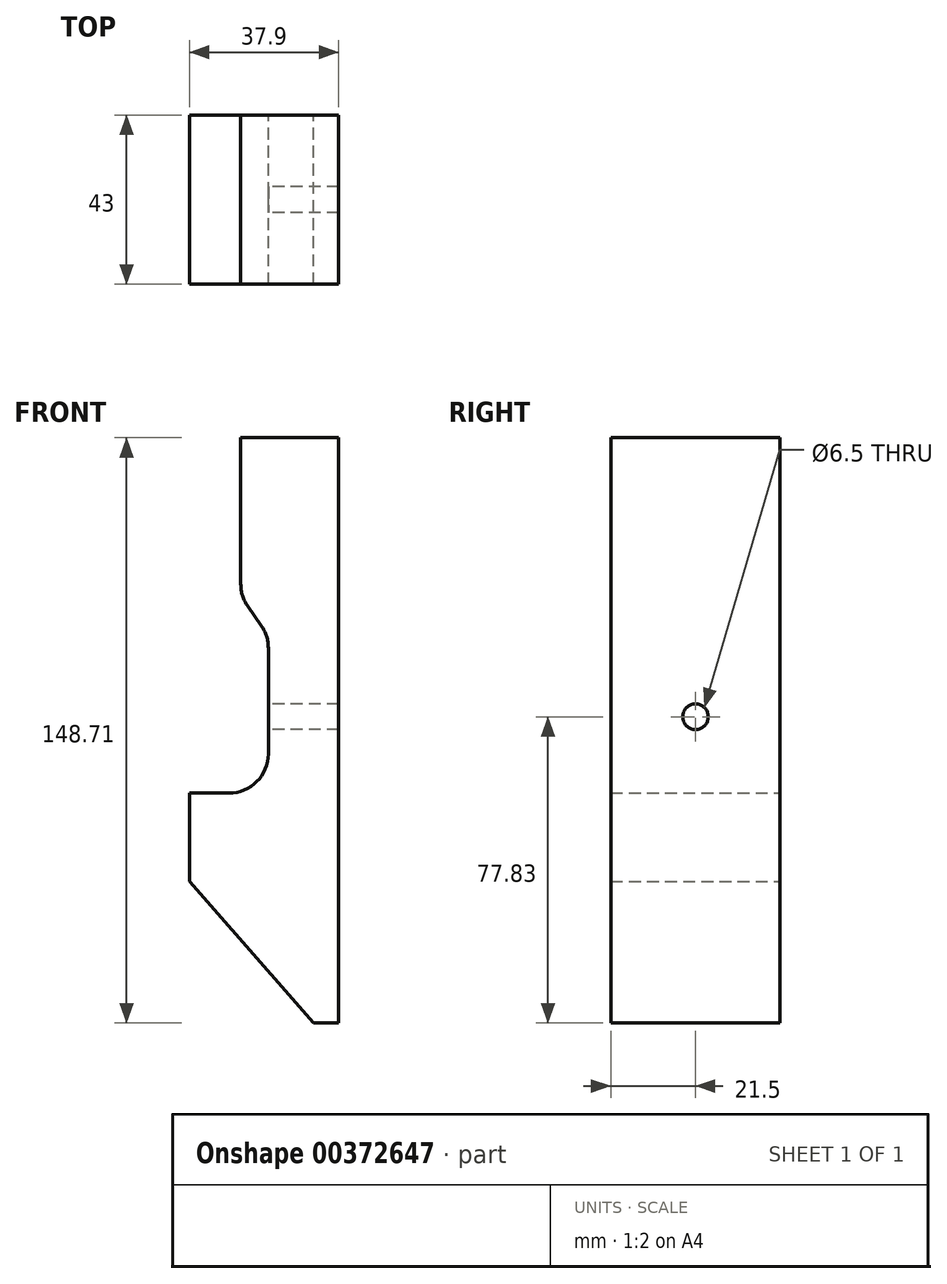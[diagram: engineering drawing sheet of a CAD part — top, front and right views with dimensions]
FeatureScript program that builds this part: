
annotation { "Feature Type Name" : "Feature", "Feature Type Description" : "" }
export const myFeature = defineFeature(function(context is Context, id is Id, definition is map)
    precondition{}
    {
        {
            var Q0;
            Q0=qCreatedBy(makeId("Front.planeOp"),FACE);
            var sketch = newSketch(context, id + "F0", { "sketchPlane" : qUnion([Q0])});
            skLineSegment(sketch, "E0", {"start": v(-20, -19.4) * mm, "end": v(0, -19.4) * mm});
            skLineSegment(sketch, "E1", {"start": v(0, 20.6) * mm, "end": v(-7, 30.6) * mm});
            skLineSegment(sketch, "E2", {"start": v(-7, 30.6) * mm, "end": v(-7, 70.88) * mm});
            skLineSegment(sketch, "E3", {"start": v(-7, 70.88) * mm, "end": v(17.9, 70.88) * mm});
            skLineSegment(sketch, "E4", {"start": v(17.9, 70.88) * mm, "end": v(17.9, -77.83) * mm});
            skLineSegment(sketch, "E5", {"start": v(17.9, -77.83) * mm, "end": v(11.45, -77.83) * mm});
            skLineSegment(sketch, "E6", {"start": v(11.45, -77.83) * mm, "end": v(-20, -41.81) * mm});
            skLineSegment(sketch, "E7", {"start": v(-20, -41.81) * mm, "end": v(-20, -19.4) * mm});
            skLineSegment(sketch, "E8", {"start": v(0, 20.6) * mm, "end": v(0, -19.4) * mm});
            skSolve(sketch);
        }
        {
            var Q0;
            Q0=makeQuery(id+"F0.imprint","IMPRINT",FACE,{"disambiguationData":[TD([[makeQuery(id+"F0.imprint","IMPRINT",EDGE,{"derivedFrom":sQuery(id+"F0.wireOp",EDGE,"E0")}),-1.0]])]});
            extrude(context, id + "F1", {"entities" : qUnion([Q0]), "depth" : 43 * mm, "offsetDistance" : 25 * mm, "symmetric" : true});
        }
        {
            var Q0;
            Q0=qCreatedBy(makeId("Right.planeOp"),FACE);
            var sketch = newSketch(context, id + "F2", { "sketchPlane" : qUnion([Q0])});
            skCircle(sketch, "E9", {"center": v(0, 0) * mm, "radius": 3.25 * mm});
            skSolve(sketch);
        }
        {
            var Q0;
            Q0 = qSketchRegion(id + "F2", true);
            extrude(context, id + "F3", {"entities" : qUnion([Q0]), "operationType" : NewBodyOperationType.REMOVE, "endBound" : BoundingType.THROUGH_ALL, "depth" : 25 * mm, "offsetDistance" : 25 * mm});
        }
        {
            var Q0;
            Q0=makeQuery(id+"F1.opExtrude","SWEPT_EDGE",EDGE,{"disambiguationData":[OSD([sQuery(id+"F0.wireOp",EDGE,"E0"),sQuery(id+"F0.wireOp",EDGE,"E8")])]});
            var Q1;
            Q1=makeQuery(id+"F1.opExtrude","SWEPT_EDGE",EDGE,{"disambiguationData":[OSD([sQuery(id+"F0.wireOp",EDGE,"E1"),sQuery(id+"F0.wireOp",EDGE,"E8")])]});
            var Q2;
            Q2=makeQuery(id+"F1.opExtrude","SWEPT_EDGE",EDGE,{"disambiguationData":[OSD([sQuery(id+"F0.wireOp",EDGE,"E1"),sQuery(id+"F0.wireOp",EDGE,"E2")])]});
            fillet(context, id + "F4", {"entities" : qUnion([Q0, Q1, Q2]), "radius" : 10 * mm, "tangentPropagation" : true, "allowEdgeOverflow" : false});
        }
    });
